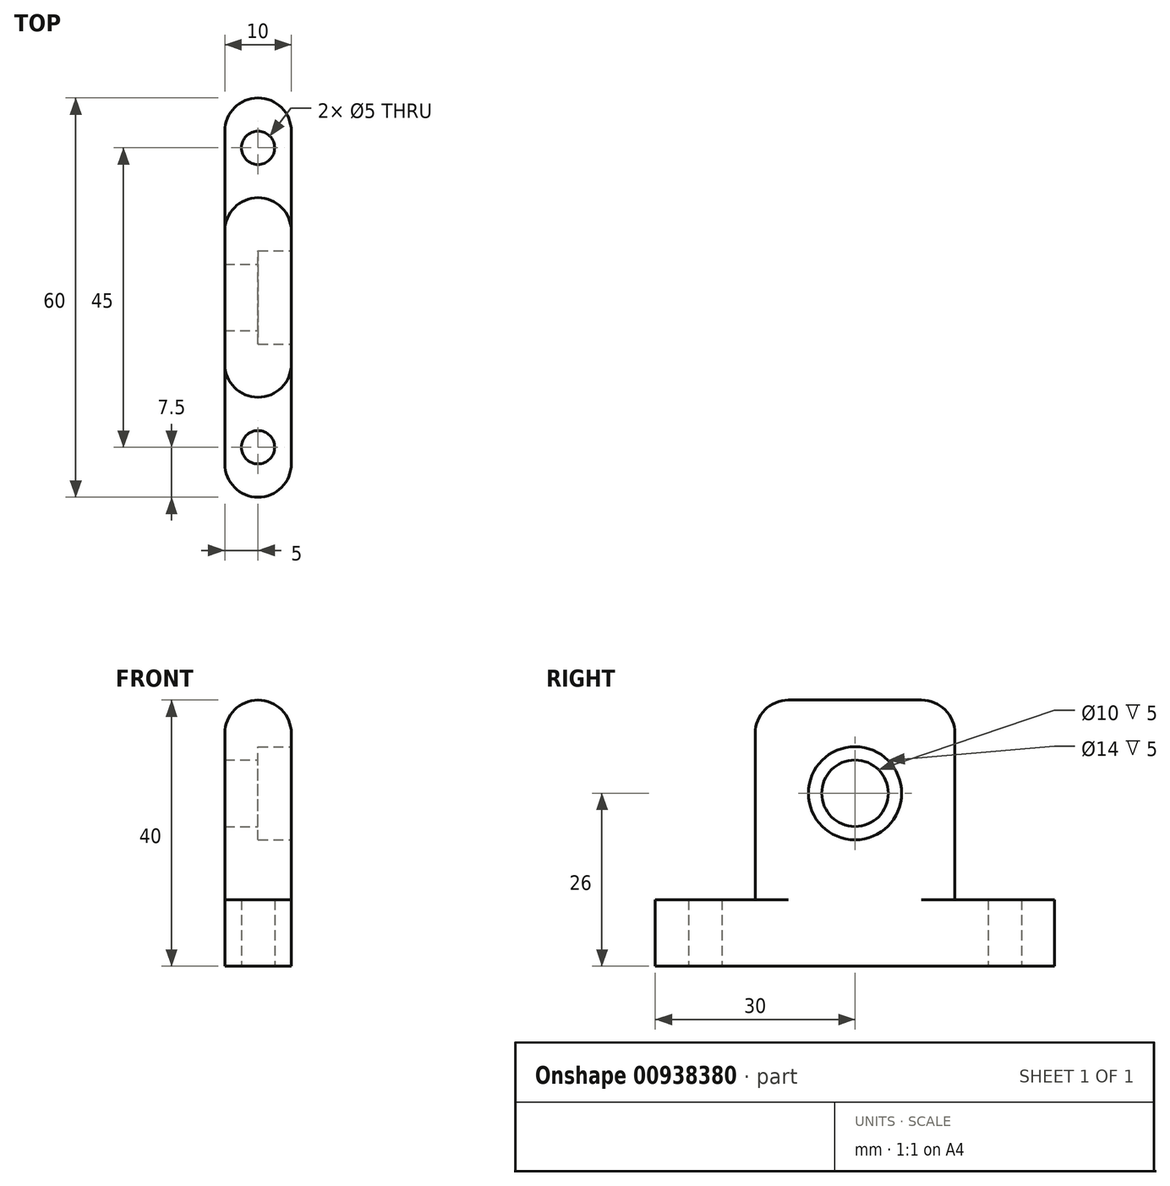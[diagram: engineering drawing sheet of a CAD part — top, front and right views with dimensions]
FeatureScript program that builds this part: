
annotation { "Feature Type Name" : "Feature", "Feature Type Description" : "" }
export const myFeature = defineFeature(function(context is Context, id is Id, definition is map)
    precondition{}
    {
        {
            var Q0;
            Q0=qCreatedBy(makeId("Top.planeOp"),FACE);
            var sketch = newSketch(context, id + "F0", { "sketchPlane" : qUnion([Q0])});
            skLineSegment(sketch, "E0.bottom", {"start": v(-5, 15) * mm, "end": v(5, 15) * mm});
            skLineSegment(sketch, "E0.top", {"start": v(-5, -45) * mm, "end": v(5, -45) * mm});
            skLineSegment(sketch, "E0.left", {"start": v(-5, 15) * mm, "end": v(-5, -45) * mm});
            skLineSegment(sketch, "E0.right", {"start": v(5, 15) * mm, "end": v(5, -45) * mm});
            skLineSegment(sketch, "E1", {"start": v(-5, 0) * mm, "end": v(5, 0) * mm});
            skLineSegment(sketch, "E2", {"start": v(5, -30) * mm, "end": v(-5, -30) * mm});
            skCircle(sketch, "E3", {"center": v(0, 7.5) * mm, "radius": 2.5 * mm});
            skCircle(sketch, "E4", {"center": v(0, -37.5) * mm, "radius": 2.5 * mm});
            skSolve(sketch);
        }
        {
            var Q0;
            {var subQ0=sQuery(id+"F0.wireOp",EDGE,"E1");Q0=makeQuery(id+"F0.imprint","IMPRINT",FACE,{"disambiguationData":[TD([[makeQuery(id+"F0.imprint","IMPRINT",EDGE,{"derivedFrom":subQ0}),-1.0]])]});}
            extrude(context, id + "F1", {"entities" : qUnion([Q0]), "depth" : 40 * mm, "offsetDistance" : 25 * mm});
        }
        {
            var Q0;
            {var subQ2=sQuery(id+"F0.wireOp",EDGE,"E0.bottom");Q0=makeQuery(id+"F0.imprint","IMPRINT",FACE,{"disambiguationData":[TD([[makeQuery(id+"F0.imprint","IMPRINT",EDGE,{"derivedFrom":subQ2}),-1.0]])]});}
            var Q1;
            {var subQ1=sQuery(id+"F0.wireOp",EDGE,"E0.top");Q1=makeQuery(id+"F0.imprint","IMPRINT",FACE,{"disambiguationData":[TD([[makeQuery(id+"F0.imprint","IMPRINT",EDGE,{"derivedFrom":subQ1}),1.0]])]});}
            extrude(context, id + "F2", {"entities" : qUnion([Q0, Q1]), "operationType" : NewBodyOperationType.ADD, "depth" : 10 * mm, "offsetDistance" : 25 * mm});
        }
        {
            var Q0;
            {var subQ0=sQuery(id+"F0.wireOp",EDGE,"E0.right");Q0=makeQuery(id+"F2.boolean.opBoolean","MERGE",FACE,{"derivedFrom":[makeQuery(id+"F1.opExtrude","SWEPT_FACE",FACE,{"disambiguationData":[OSD([subQ0])]}),makeQuery(id+"F2.opExtrude","SWEPT_FACE",FACE,{"disambiguationData":[OSD([subQ0]),TDD([makeQuery(id+"F0.imprint","IMPRINT",EDGE,{"disambiguationData":[TD([[makeQuery(id+"F0.imprint","INTERSECT",VERTEX,{"derivedFrom":[sQuery(id+"F0.wireOp",EDGE,"E0.bottom"),subQ0]}),-1.0]])],"derivedFrom":subQ0})])]}),makeQuery(id+"F2.opExtrude","SWEPT_FACE",FACE,{"disambiguationData":[OSD([subQ0]),TDD([makeQuery(id+"F0.imprint","IMPRINT",EDGE,{"disambiguationData":[TD([[makeQuery(id+"F0.imprint","INTERSECT",VERTEX,{"derivedFrom":[sQuery(id+"F0.wireOp",EDGE,"E0.top"),subQ0]}),1.0]])],"derivedFrom":subQ0})])]})]});}
            var sketch = newSketch(context, id + "F3", { "sketchPlane" : qUnion([Q0])});
            skCircle(sketch, "E5", {"center": v(-15, 26) * mm, "radius": 7 * mm});
            skCircle(sketch, "E6", {"center": v(-15, 26) * mm, "radius": 5 * mm});
            skSolve(sketch);
        }
        {
            var Q0;
            Q0=makeQuery(id+"F3.imprint","IMPRINT",FACE,{"disambiguationData":[TD([[makeQuery(id+"F3.imprint","IMPRINT",EDGE,{"derivedFrom":sQuery(id+"F3.wireOp",EDGE,"E6")}),1.0]])]});
            extrude(context, id + "F4", {"entities" : qUnion([Q0]), "operationType" : NewBodyOperationType.REMOVE, "oppositeDirection" : true, "depth" : 25 * mm, "offsetDistance" : 25 * mm});
        }
        {
            var Q0;
            Q0=makeQuery(id+"F3.imprint","IMPRINT",FACE,{"disambiguationData":[TD([[makeQuery(id+"F3.imprint","IMPRINT",EDGE,{"derivedFrom":sQuery(id+"F3.wireOp",EDGE,"E5")}),1.0]])]});
            extrude(context, id + "F5", {"entities" : qUnion([Q0]), "operationType" : NewBodyOperationType.REMOVE, "oppositeDirection" : true, "depth" : 5 * mm, "offsetDistance" : 25 * mm});
        }
        {
            var Q0;
            Q0=makeQuery(id+"F1.opExtrude","CAP_EDGE",EDGE,{"disambiguationData":[OSD([sQuery(id+"F0.wireOp",EDGE,"E2")])],"isStart":false});
            var Q1;
            Q1=makeQuery(id+"F1.opExtrude","CAP_EDGE",EDGE,{"disambiguationData":[OSD([sQuery(id+"F0.wireOp",EDGE,"E0.right")])],"isStart":false});
            var Q2;
            Q2=makeQuery(id+"F1.opExtrude","CAP_FACE",FACE,{"disambiguationData":[OSD([sQuery(id+"F0.wireOp",EDGE,"E0.left"),sQuery(id+"F0.wireOp",EDGE,"E0.right"),sQuery(id+"F0.wireOp",EDGE,"E1"),sQuery(id+"F0.wireOp",EDGE,"E2")])],"isStart":false});
            var Q3;
            Q3=makeQuery(id+"F1.opExtrude","SWEPT_EDGE",EDGE,{"disambiguationData":[OSD([sQuery(id+"F0.wireOp",EDGE,"E0.right"),sQuery(id+"F0.wireOp",EDGE,"E1")])]});
            var Q4;
            Q4=makeQuery(id+"F1.opExtrude","SWEPT_EDGE",EDGE,{"disambiguationData":[OSD([sQuery(id+"F0.wireOp",EDGE,"E0.right"),sQuery(id+"F0.wireOp",EDGE,"E2")])]});
            var Q5;
            Q5=makeQuery(id+"F1.opExtrude","SWEPT_EDGE",EDGE,{"disambiguationData":[OSD([sQuery(id+"F0.wireOp",EDGE,"E0.left"),sQuery(id+"F0.wireOp",EDGE,"E2")])]});
            var Q6;
            Q6=makeQuery(id+"F1.opExtrude","SWEPT_EDGE",EDGE,{"disambiguationData":[OSD([sQuery(id+"F0.wireOp",EDGE,"E0.left"),sQuery(id+"F0.wireOp",EDGE,"E1")])]});
            fillet(context, id + "F6", {"entities" : qUnion([Q0, Q1, Q2, Q3, Q4, Q5, Q6]), "radius" : 5 * mm, "tangentPropagation" : true, "allowEdgeOverflow" : false});
        }
        {
            var Q0;
            Q0=makeQuery(id+"F2.opExtrude","SWEPT_EDGE",EDGE,{"disambiguationData":[OSD([sQuery(id+"F0.wireOp",EDGE,"E0.bottom"),sQuery(id+"F0.wireOp",EDGE,"E0.right")])]});
            var Q1;
            Q1=makeQuery(id+"F2.opExtrude","SWEPT_EDGE",EDGE,{"disambiguationData":[OSD([sQuery(id+"F0.wireOp",EDGE,"E0.bottom"),sQuery(id+"F0.wireOp",EDGE,"E0.left")])]});
            var Q2;
            Q2=makeQuery(id+"F2.opExtrude","SWEPT_EDGE",EDGE,{"disambiguationData":[OSD([sQuery(id+"F0.wireOp",EDGE,"E0.top"),sQuery(id+"F0.wireOp",EDGE,"E0.right")])]});
            var Q3;
            Q3=makeQuery(id+"F2.opExtrude","SWEPT_EDGE",EDGE,{"disambiguationData":[OSD([sQuery(id+"F0.wireOp",EDGE,"E0.top"),sQuery(id+"F0.wireOp",EDGE,"E0.left")])]});
            fillet(context, id + "F7", {"entities" : qUnion([Q0, Q1, Q2, Q3]), "radius" : 5 * mm, "tangentPropagation" : true, "allowEdgeOverflow" : false});
        }
    });
